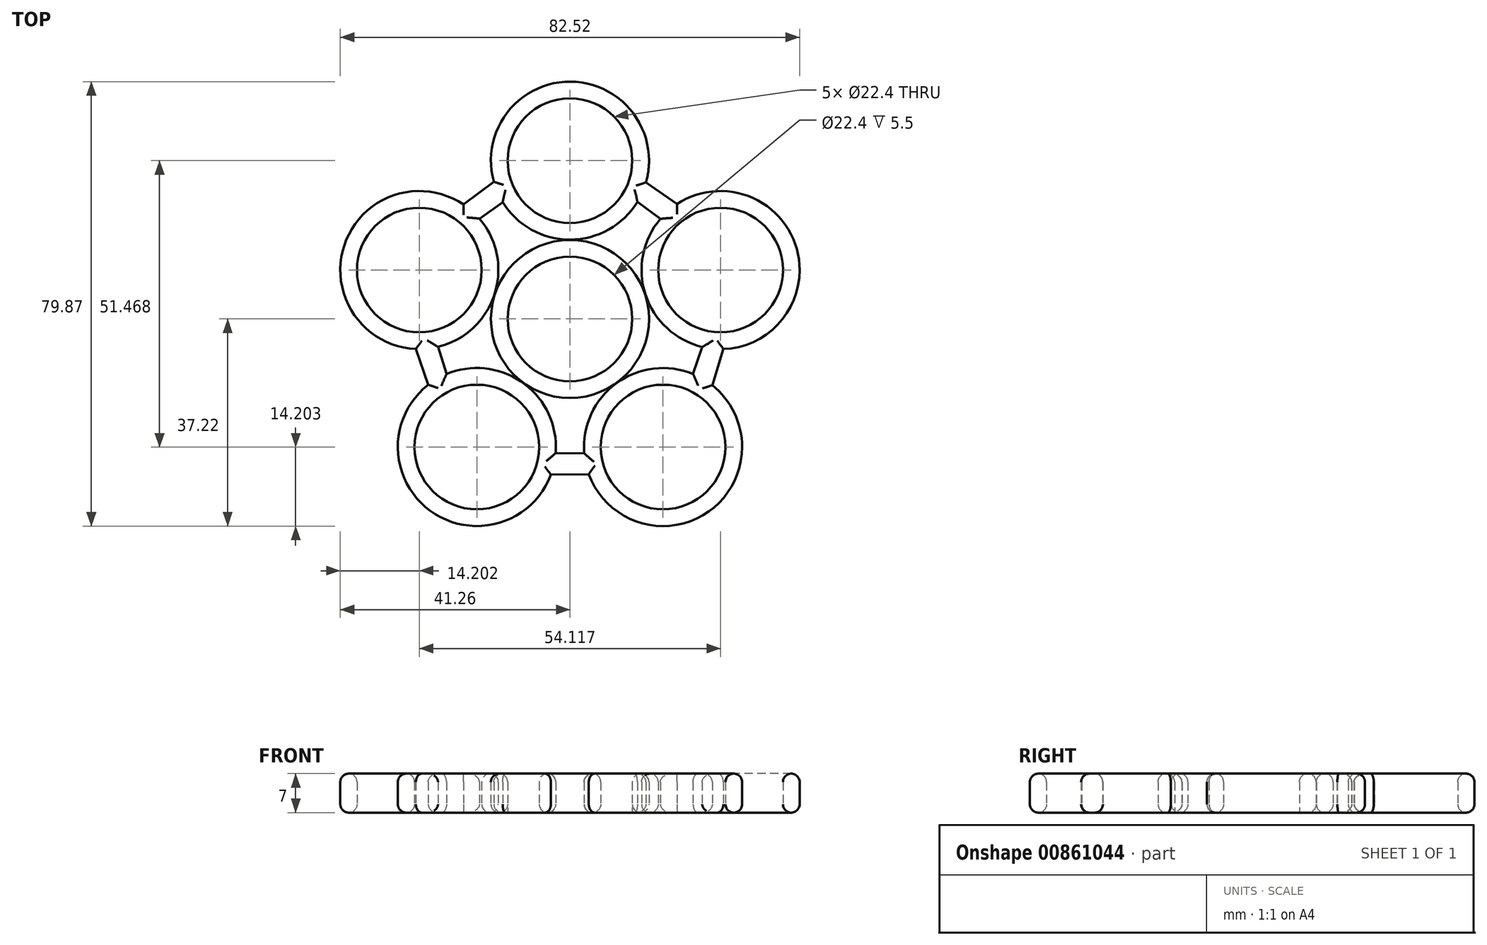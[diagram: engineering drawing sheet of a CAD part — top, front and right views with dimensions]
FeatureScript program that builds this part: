
annotation { "Feature Type Name" : "Feature", "Feature Type Description" : "" }
export const myFeature = defineFeature(function(context is Context, id is Id, definition is map)
    precondition{}
    {
        {
            var Q0;
            Q0=qCreatedBy(makeId("Top.planeOp"),FACE);
            var sketch = newSketch(context, id + "F0", { "sketchPlane" : qUnion([Q0])});
            skCircle(sketch, "E0", {"center": v(0, 0) * mm, "radius": 11.2 * mm});
            skCircle(sketch, "E1", {"center": v(0, 0) * mm, "radius": 14.2 * mm});
            skCircle(sketch, "E2", {"center": v(0, 28.45) * mm, "radius": 11.2 * mm});
            skCircle(sketch, "E3", {"center": v(0, 28.45) * mm, "radius": 14.2 * mm});
            skCircle(sketch, "E4.1.0", {"center": v(-27.06, 8.8) * mm, "radius": 14.2 * mm});
            skCircle(sketch, "E4.1.1", {"center": v(-27.06, 8.8) * mm, "radius": 11.2 * mm});
            skCircle(sketch, "E4.2.0", {"center": v(-16.72, -23.02) * mm, "radius": 14.2 * mm});
            skCircle(sketch, "E4.2.1", {"center": v(-16.72, -23.02) * mm, "radius": 11.2 * mm});
            skCircle(sketch, "E4.3.0", {"center": v(16.72, -23.02) * mm, "radius": 14.2 * mm});
            skCircle(sketch, "E4.3.1", {"center": v(16.72, -23.02) * mm, "radius": 11.2 * mm});
            skCircle(sketch, "E4.4.0", {"center": v(27.06, 8.8) * mm, "radius": 14.2 * mm});
            skCircle(sketch, "E4.4.1", {"center": v(27.06, 8.8) * mm, "radius": 11.2 * mm});
            skLineSegment(sketch, "E5", {"start": v(-19.13, 20.57) * mm, "end": v(-13.69, 24.66) * mm});
            skLineSegment(sketch, "E6", {"start": v(-16.27, 18.03) * mm, "end": v(-12.09, 21) * mm});
            skLineSegment(sketch, "E7.1.0", {"start": v(-25.48, -11.84) * mm, "end": v(-27.69, -5.4) * mm});
            skLineSegment(sketch, "E7.1.1", {"start": v(-22.18, -9.9) * mm, "end": v(-23.7, -5) * mm});
            skLineSegment(sketch, "E7.2.0", {"start": v(3.39, -27.9) * mm, "end": v(-3.43, -28) * mm});
            skLineSegment(sketch, "E7.2.1", {"start": v(2.57, -24.15) * mm, "end": v(-2.56, -24.1) * mm});
            skLineSegment(sketch, "E7.3.0", {"start": v(27.57, -5.4) * mm, "end": v(25.57, -11.9) * mm});
            skLineSegment(sketch, "E7.3.1", {"start": v(23.76, -5.02) * mm, "end": v(22.12, -9.88) * mm});
            skLineSegment(sketch, "E7.4.0", {"start": v(13.65, 24.55) * mm, "end": v(19.23, 20.64) * mm});
            skLineSegment(sketch, "E7.4.1", {"start": v(12.12, 21.05) * mm, "end": v(16.24, 17.99) * mm});
            skSolve(sketch);
        }
        {
            var Q0;
            Q0 = qSketchRegion(id + "F0", true);
            var Q1;
            Q1=makeQuery(id+"F0.imprint","IMPRINT",FACE,{"disambiguationData":[TD([[makeQuery(id+"F0.imprint","IMPRINT",EDGE,{"derivedFrom":sQuery(id+"F0.wireOp",EDGE,"E0")}),-1.0]])]});
            extrude(context, id + "F1", {"entities" : qUnion([Q0, Q1]), "depth" : 7 * mm, "offsetDistance" : 25 * mm});
        }
        {
            var Q0;
            Q0=makeQuery(id+"F1.opExtrude","CAP_EDGE",EDGE,{"disambiguationData":[OSD([sQuery(id+"F0.wireOp",EDGE,"E7.4.0")])],"isStart":true});
            var Q1;
            {var subQ0=sQuery(id+"F0.wireOp",EDGE,"E3");Q1=makeQuery(id+"F1.opExtrude","CAP_EDGE",EDGE,{"disambiguationData":[OSD([subQ0]),TDD([makeQuery(id+"F0.imprint","IMPRINT",EDGE,{"disambiguationData":[TD([[makeQuery(id+"F0.imprint","INTERSECT",VERTEX,{"derivedFrom":[subQ0,sQuery(id+"F0.wireOp",EDGE,"E5")]}),1.0]])],"derivedFrom":subQ0})])],"isStart":true});}
            var Q2;
            Q2=makeQuery(id+"F1.opExtrude","CAP_EDGE",EDGE,{"disambiguationData":[OSD([sQuery(id+"F0.wireOp",EDGE,"E6")])],"isStart":true});
            var Q3;
            {var subQ0=sQuery(id+"F0.wireOp",EDGE,"E4.1.0");Q3=makeQuery(id+"F1.opExtrude","CAP_EDGE",EDGE,{"disambiguationData":[OSD([subQ0]),TDD([makeQuery(id+"F0.imprint","IMPRINT",EDGE,{"disambiguationData":[TD([[makeQuery(id+"F0.imprint","INTERSECT",VERTEX,{"derivedFrom":[subQ0,sQuery(id+"F0.wireOp",EDGE,"E5")]}),-1.0]])],"derivedFrom":subQ0})])],"isStart":true});}
            var Q4;
            Q4=makeQuery(id+"F1.opExtrude","CAP_EDGE",EDGE,{"disambiguationData":[OSD([sQuery(id+"F0.wireOp",EDGE,"E5")])],"isStart":true});
            var Q5;
            {var subQ0=sQuery(id+"F0.wireOp",EDGE,"E3");Q5=makeQuery(id+"F1.opExtrude","CAP_EDGE",EDGE,{"disambiguationData":[OSD([subQ0]),TDD([makeQuery(id+"F0.imprint","IMPRINT",EDGE,{"disambiguationData":[TD([[makeQuery(id+"F0.imprint","INTERSECT",VERTEX,{"derivedFrom":[subQ0,sQuery(id+"F0.wireOp",EDGE,"E6")]}),-1.0]])],"derivedFrom":subQ0})])],"isStart":true});}
            var Q6;
            {var subQ0=sQuery(id+"F0.wireOp",EDGE,"E4.4.0");Q6=makeQuery(id+"F1.opExtrude","CAP_EDGE",EDGE,{"disambiguationData":[OSD([subQ0]),TDD([makeQuery(id+"F0.imprint","IMPRINT",EDGE,{"disambiguationData":[TD([[makeQuery(id+"F0.imprint","INTERSECT",VERTEX,{"derivedFrom":[subQ0,sQuery(id+"F0.wireOp",EDGE,"E7.3.1")]}),1.0]])],"derivedFrom":subQ0})])],"isStart":true});}
            var Q7;
            Q7=makeQuery(id+"F1.opExtrude","CAP_EDGE",EDGE,{"disambiguationData":[OSD([sQuery(id+"F0.wireOp",EDGE,"E7.4.1")])],"isStart":true});
            var Q8;
            Q8=makeQuery(id+"F1.opExtrude","CAP_EDGE",EDGE,{"disambiguationData":[OSD([sQuery(id+"F0.wireOp",EDGE,"E1")])],"isStart":true});
            var Q9;
            {var subQ0=sQuery(id+"F0.wireOp",EDGE,"E4.1.0");Q9=makeQuery(id+"F1.opExtrude","CAP_EDGE",EDGE,{"disambiguationData":[OSD([subQ0]),TDD([makeQuery(id+"F0.imprint","IMPRINT",EDGE,{"disambiguationData":[TD([[makeQuery(id+"F0.imprint","INTERSECT",VERTEX,{"derivedFrom":[subQ0,sQuery(id+"F0.wireOp",EDGE,"E6")]}),1.0]])],"derivedFrom":subQ0})])],"isStart":true});}
            var Q10;
            Q10=makeQuery(id+"F1.opExtrude","CAP_EDGE",EDGE,{"disambiguationData":[OSD([sQuery(id+"F0.wireOp",EDGE,"E7.1.1")])],"isStart":true});
            var Q11;
            {var subQ0=sQuery(id+"F0.wireOp",EDGE,"E4.2.0");Q11=makeQuery(id+"F1.opExtrude","CAP_EDGE",EDGE,{"disambiguationData":[OSD([subQ0]),TDD([makeQuery(id+"F0.imprint","IMPRINT",EDGE,{"disambiguationData":[TD([[makeQuery(id+"F0.imprint","INTERSECT",VERTEX,{"derivedFrom":[subQ0,sQuery(id+"F0.wireOp",EDGE,"E7.1.0")]}),-1.0]])],"derivedFrom":subQ0})])],"isStart":true});}
            var Q12;
            Q12=makeQuery(id+"F1.opExtrude","CAP_EDGE",EDGE,{"disambiguationData":[OSD([sQuery(id+"F0.wireOp",EDGE,"E7.1.0")])],"isStart":true});
            var Q13;
            Q13=makeQuery(id+"F1.opExtrude","CAP_EDGE",EDGE,{"disambiguationData":[OSD([sQuery(id+"F0.wireOp",EDGE,"E7.2.1")])],"isStart":true});
            var Q14;
            {var subQ0=sQuery(id+"F0.wireOp",EDGE,"E4.2.0");Q14=makeQuery(id+"F1.opExtrude","CAP_EDGE",EDGE,{"disambiguationData":[OSD([subQ0]),TDD([makeQuery(id+"F0.imprint","IMPRINT",EDGE,{"disambiguationData":[TD([[makeQuery(id+"F0.imprint","INTERSECT",VERTEX,{"derivedFrom":[subQ0,sQuery(id+"F0.wireOp",EDGE,"E7.1.1")]}),1.0]])],"derivedFrom":subQ0})])],"isStart":true});}
            var Q15;
            {var subQ0=sQuery(id+"F0.wireOp",EDGE,"E4.3.0");Q15=makeQuery(id+"F1.opExtrude","CAP_EDGE",EDGE,{"disambiguationData":[OSD([subQ0]),TDD([makeQuery(id+"F0.imprint","IMPRINT",EDGE,{"disambiguationData":[TD([[makeQuery(id+"F0.imprint","INTERSECT",VERTEX,{"derivedFrom":[subQ0,sQuery(id+"F0.wireOp",EDGE,"E7.2.1")]}),1.0]])],"derivedFrom":subQ0})])],"isStart":true});}
            var Q16;
            Q16=makeQuery(id+"F1.opExtrude","CAP_EDGE",EDGE,{"disambiguationData":[OSD([sQuery(id+"F0.wireOp",EDGE,"E7.3.1")])],"isStart":true});
            var Q17;
            {var subQ0=sQuery(id+"F0.wireOp",EDGE,"E4.3.0");Q17=makeQuery(id+"F1.opExtrude","CAP_EDGE",EDGE,{"disambiguationData":[OSD([subQ0]),TDD([makeQuery(id+"F0.imprint","IMPRINT",EDGE,{"disambiguationData":[TD([[makeQuery(id+"F0.imprint","INTERSECT",VERTEX,{"derivedFrom":[subQ0,sQuery(id+"F0.wireOp",EDGE,"E7.2.0")]}),-1.0]])],"derivedFrom":subQ0})])],"isStart":true});}
            var Q18;
            Q18=makeQuery(id+"F1.opExtrude","CAP_EDGE",EDGE,{"disambiguationData":[OSD([sQuery(id+"F0.wireOp",EDGE,"E7.3.0")])],"isStart":true});
            var Q19;
            Q19=makeQuery(id+"F1.opExtrude","CAP_EDGE",EDGE,{"disambiguationData":[OSD([sQuery(id+"F0.wireOp",EDGE,"E7.2.0")])],"isStart":true});
            var Q20;
            {var subQ0=sQuery(id+"F0.wireOp",EDGE,"E4.4.0");Q20=makeQuery(id+"F1.opExtrude","CAP_EDGE",EDGE,{"disambiguationData":[OSD([subQ0]),TDD([makeQuery(id+"F0.imprint","IMPRINT",EDGE,{"disambiguationData":[TD([[makeQuery(id+"F0.imprint","INTERSECT",VERTEX,{"derivedFrom":[subQ0,sQuery(id+"F0.wireOp",EDGE,"E7.3.0")]}),-1.0]])],"derivedFrom":subQ0})])],"isStart":true});}
            var Q21;
            Q21=makeQuery(id+"F1.opExtrude","CAP_EDGE",EDGE,{"disambiguationData":[OSD([sQuery(id+"F0.wireOp",EDGE,"E2")])],"isStart":true});
            var Q22;
            Q22=makeQuery(id+"F1.opExtrude","CAP_EDGE",EDGE,{"disambiguationData":[OSD([sQuery(id+"F0.wireOp",EDGE,"E4.4.1")])],"isStart":true});
            var Q23;
            Q23=makeQuery(id+"F1.opExtrude","CAP_EDGE",EDGE,{"disambiguationData":[OSD([sQuery(id+"F0.wireOp",EDGE,"E4.1.1")])],"isStart":true});
            var Q24;
            Q24=makeQuery(id+"F1.opExtrude","CAP_EDGE",EDGE,{"disambiguationData":[OSD([sQuery(id+"F0.wireOp",EDGE,"E4.2.1")])],"isStart":true});
            var Q25;
            Q25=makeQuery(id+"F1.opExtrude","CAP_EDGE",EDGE,{"disambiguationData":[OSD([sQuery(id+"F0.wireOp",EDGE,"E4.3.1")])],"isStart":true});
            fillet(context, id + "F2", {"entities" : qUnion([Q0, Q1, Q2, Q3, Q4, Q5, Q6, Q7, Q8, Q9, Q10, Q11, Q12, Q13, Q14, Q15, Q16, Q17, Q18, Q19, Q20, Q21, Q22, Q23, Q24, Q25]), "radius" : 1.5 * mm, "tangentPropagation" : true, "allowEdgeOverflow" : false});
        }
        {
            var Q0;
            {var subQ0=sQuery(id+"F0.wireOp",EDGE,"E4.1.0");Q0=makeQuery(id+"F1.opExtrude","CAP_EDGE",EDGE,{"disambiguationData":[OSD([subQ0]),TDD([makeQuery(id+"F0.imprint","IMPRINT",EDGE,{"disambiguationData":[TD([[makeQuery(id+"F0.imprint","INTERSECT",VERTEX,{"derivedFrom":[subQ0,sQuery(id+"F0.wireOp",EDGE,"E5")]}),-1.0]])],"derivedFrom":subQ0})])],"isStart":false});}
            var Q1;
            {var subQ0=sQuery(id+"F0.wireOp",EDGE,"E4.2.0");Q1=makeQuery(id+"F1.opExtrude","CAP_EDGE",EDGE,{"disambiguationData":[OSD([subQ0]),TDD([makeQuery(id+"F0.imprint","IMPRINT",EDGE,{"disambiguationData":[TD([[makeQuery(id+"F0.imprint","INTERSECT",VERTEX,{"derivedFrom":[subQ0,sQuery(id+"F0.wireOp",EDGE,"E7.1.0")]}),-1.0]])],"derivedFrom":subQ0})])],"isStart":false});}
            var Q2;
            {var subQ0=sQuery(id+"F0.wireOp",EDGE,"E4.3.0");Q2=makeQuery(id+"F1.opExtrude","CAP_EDGE",EDGE,{"disambiguationData":[OSD([subQ0]),TDD([makeQuery(id+"F0.imprint","IMPRINT",EDGE,{"disambiguationData":[TD([[makeQuery(id+"F0.imprint","INTERSECT",VERTEX,{"derivedFrom":[subQ0,sQuery(id+"F0.wireOp",EDGE,"E7.2.0")]}),-1.0]])],"derivedFrom":subQ0})])],"isStart":false});}
            var Q3;
            {var subQ0=sQuery(id+"F0.wireOp",EDGE,"E4.4.0");Q3=makeQuery(id+"F1.opExtrude","CAP_EDGE",EDGE,{"disambiguationData":[OSD([subQ0]),TDD([makeQuery(id+"F0.imprint","IMPRINT",EDGE,{"disambiguationData":[TD([[makeQuery(id+"F0.imprint","INTERSECT",VERTEX,{"derivedFrom":[subQ0,sQuery(id+"F0.wireOp",EDGE,"E7.3.0")]}),-1.0]])],"derivedFrom":subQ0})])],"isStart":false});}
            var Q4;
            Q4=makeQuery(id+"F1.opExtrude","CAP_EDGE",EDGE,{"disambiguationData":[OSD([sQuery(id+"F0.wireOp",EDGE,"E2")])],"isStart":false});
            var Q5;
            Q5=makeQuery(id+"F1.opExtrude","CAP_EDGE",EDGE,{"disambiguationData":[OSD([sQuery(id+"F0.wireOp",EDGE,"E4.4.1")])],"isStart":false});
            var Q6;
            Q6=makeQuery(id+"F1.opExtrude","CAP_EDGE",EDGE,{"disambiguationData":[OSD([sQuery(id+"F0.wireOp",EDGE,"E4.1.1")])],"isStart":false});
            var Q7;
            Q7=makeQuery(id+"F1.opExtrude","CAP_EDGE",EDGE,{"disambiguationData":[OSD([sQuery(id+"F0.wireOp",EDGE,"E0")])],"isStart":false});
            var Q8;
            Q8=makeQuery(id+"F1.opExtrude","CAP_EDGE",EDGE,{"disambiguationData":[OSD([sQuery(id+"F0.wireOp",EDGE,"E1")])],"isStart":false});
            var Q9;
            {var subQ0=sQuery(id+"F0.wireOp",EDGE,"E3");Q9=makeQuery(id+"F1.opExtrude","CAP_EDGE",EDGE,{"disambiguationData":[OSD([subQ0]),TDD([makeQuery(id+"F0.imprint","IMPRINT",EDGE,{"disambiguationData":[TD([[makeQuery(id+"F0.imprint","INTERSECT",VERTEX,{"derivedFrom":[subQ0,sQuery(id+"F0.wireOp",EDGE,"E6")]}),-1.0]])],"derivedFrom":subQ0})])],"isStart":false});}
            var Q10;
            Q10=makeQuery(id+"F1.opExtrude","CAP_EDGE",EDGE,{"disambiguationData":[OSD([sQuery(id+"F0.wireOp",EDGE,"E7.4.0")])],"isStart":false});
            var Q11;
            {var subQ0=sQuery(id+"F0.wireOp",EDGE,"E3");Q11=makeQuery(id+"F1.opExtrude","CAP_EDGE",EDGE,{"disambiguationData":[OSD([subQ0]),TDD([makeQuery(id+"F0.imprint","IMPRINT",EDGE,{"disambiguationData":[TD([[makeQuery(id+"F0.imprint","INTERSECT",VERTEX,{"derivedFrom":[subQ0,sQuery(id+"F0.wireOp",EDGE,"E5")]}),1.0]])],"derivedFrom":subQ0})])],"isStart":false});}
            var Q12;
            Q12=makeQuery(id+"F1.opExtrude","CAP_EDGE",EDGE,{"disambiguationData":[OSD([sQuery(id+"F0.wireOp",EDGE,"E5")])],"isStart":false});
            var Q13;
            {var subQ0=sQuery(id+"F0.wireOp",EDGE,"E4.1.0");Q13=makeQuery(id+"F1.opExtrude","CAP_EDGE",EDGE,{"disambiguationData":[OSD([subQ0]),TDD([makeQuery(id+"F0.imprint","IMPRINT",EDGE,{"disambiguationData":[TD([[makeQuery(id+"F0.imprint","INTERSECT",VERTEX,{"derivedFrom":[subQ0,sQuery(id+"F0.wireOp",EDGE,"E6")]}),1.0]])],"derivedFrom":subQ0})])],"isStart":false});}
            var Q14;
            Q14=makeQuery(id+"F1.opExtrude","CAP_EDGE",EDGE,{"disambiguationData":[OSD([sQuery(id+"F0.wireOp",EDGE,"E7.1.0")])],"isStart":false});
            var Q15;
            {var subQ0=sQuery(id+"F0.wireOp",EDGE,"E4.2.0");Q15=makeQuery(id+"F1.opExtrude","CAP_EDGE",EDGE,{"disambiguationData":[OSD([subQ0]),TDD([makeQuery(id+"F0.imprint","IMPRINT",EDGE,{"disambiguationData":[TD([[makeQuery(id+"F0.imprint","INTERSECT",VERTEX,{"derivedFrom":[subQ0,sQuery(id+"F0.wireOp",EDGE,"E7.1.1")]}),1.0]])],"derivedFrom":subQ0})])],"isStart":false});}
            var Q16;
            Q16=makeQuery(id+"F1.opExtrude","CAP_EDGE",EDGE,{"disambiguationData":[OSD([sQuery(id+"F0.wireOp",EDGE,"E7.2.1")])],"isStart":false});
            var Q17;
            {var subQ0=sQuery(id+"F0.wireOp",EDGE,"E4.3.0");Q17=makeQuery(id+"F1.opExtrude","CAP_EDGE",EDGE,{"disambiguationData":[OSD([subQ0]),TDD([makeQuery(id+"F0.imprint","IMPRINT",EDGE,{"disambiguationData":[TD([[makeQuery(id+"F0.imprint","INTERSECT",VERTEX,{"derivedFrom":[subQ0,sQuery(id+"F0.wireOp",EDGE,"E7.2.1")]}),1.0]])],"derivedFrom":subQ0})])],"isStart":false});}
            var Q18;
            {var subQ0=sQuery(id+"F0.wireOp",EDGE,"E4.4.0");Q18=makeQuery(id+"F1.opExtrude","CAP_EDGE",EDGE,{"disambiguationData":[OSD([subQ0]),TDD([makeQuery(id+"F0.imprint","IMPRINT",EDGE,{"disambiguationData":[TD([[makeQuery(id+"F0.imprint","INTERSECT",VERTEX,{"derivedFrom":[subQ0,sQuery(id+"F0.wireOp",EDGE,"E7.3.1")]}),1.0]])],"derivedFrom":subQ0})])],"isStart":false});}
            var Q19;
            Q19=makeQuery(id+"F1.opExtrude","CAP_EDGE",EDGE,{"disambiguationData":[OSD([sQuery(id+"F0.wireOp",EDGE,"E7.4.1")])],"isStart":false});
            var Q20;
            Q20=makeQuery(id+"F1.opExtrude","CAP_EDGE",EDGE,{"disambiguationData":[OSD([sQuery(id+"F0.wireOp",EDGE,"E6")])],"isStart":false});
            var Q21;
            Q21=makeQuery(id+"F1.opExtrude","CAP_EDGE",EDGE,{"disambiguationData":[OSD([sQuery(id+"F0.wireOp",EDGE,"E7.1.1")])],"isStart":false});
            var Q22;
            Q22=makeQuery(id+"F1.opExtrude","CAP_EDGE",EDGE,{"disambiguationData":[OSD([sQuery(id+"F0.wireOp",EDGE,"E7.3.1")])],"isStart":false});
            var Q23;
            Q23=makeQuery(id+"F1.opExtrude","CAP_EDGE",EDGE,{"disambiguationData":[OSD([sQuery(id+"F0.wireOp",EDGE,"E7.3.0")])],"isStart":false});
            var Q24;
            Q24=makeQuery(id+"F1.opExtrude","CAP_EDGE",EDGE,{"disambiguationData":[OSD([sQuery(id+"F0.wireOp",EDGE,"E4.3.1")])],"isStart":false});
            var Q25;
            Q25=makeQuery(id+"F1.opExtrude","CAP_EDGE",EDGE,{"disambiguationData":[OSD([sQuery(id+"F0.wireOp",EDGE,"E4.2.1")])],"isStart":false});
            var Q26;
            Q26=makeQuery(id+"F1.opExtrude","CAP_EDGE",EDGE,{"disambiguationData":[OSD([sQuery(id+"F0.wireOp",EDGE,"E7.2.0")])],"isStart":false});
            fillet(context, id + "F3", {"entities" : qUnion([Q0, Q1, Q2, Q3, Q4, Q5, Q6, Q7, Q8, Q9, Q10, Q11, Q12, Q13, Q14, Q15, Q16, Q17, Q18, Q19, Q20, Q21, Q22, Q23, Q24, Q25, Q26]), "radius" : 1.5 * mm, "tangentPropagation" : true, "allowEdgeOverflow" : false});
        }
    });
